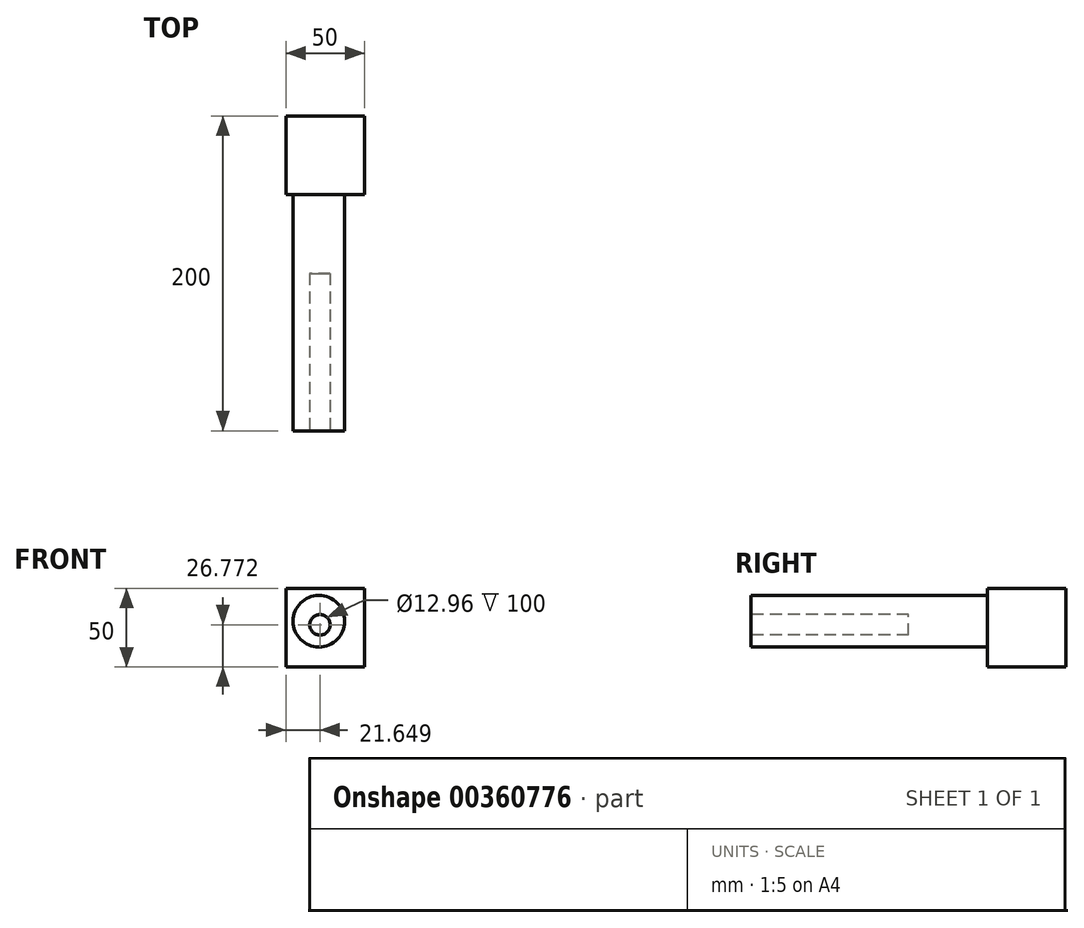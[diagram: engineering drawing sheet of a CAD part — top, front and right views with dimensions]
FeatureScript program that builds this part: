
annotation { "Feature Type Name" : "Feature", "Feature Type Description" : "" }
export const myFeature = defineFeature(function(context is Context, id is Id, definition is map)
    precondition{}
    {
        {
            var Q0;
            Q0=qCreatedBy(makeId("Top.planeOp"),FACE);
            var sketch = newSketch(context, id + "F0", { "sketchPlane" : qUnion([Q0])});
            skLineSegment(sketch, "E0.bottom", {"start": v(0, 0) * mm, "end": v(50, 0) * mm});
            skLineSegment(sketch, "E0.top", {"start": v(0, 50) * mm, "end": v(50, 50) * mm});
            skLineSegment(sketch, "E0.left", {"start": v(0, 0) * mm, "end": v(0, 50) * mm});
            skLineSegment(sketch, "E0.right", {"start": v(50, 0) * mm, "end": v(50, 50) * mm});
            skSolve(sketch);
        }
        {
            var Q0;
            Q0=makeQuery(id+"F0.imprint","IMPRINT",FACE,{"disambiguationData":[TD([[makeQuery(id+"F0.imprint","IMPRINT",EDGE,{"derivedFrom":sQuery(id+"F0.wireOp",EDGE,"E0.bottom")}),1.0]])]});
            extrude(context, id + "F1", {"entities" : qUnion([Q0]), "depth" : 50 * mm});
        }
        {
            var Q0;
            Q0=makeQuery(id+"F1.opExtrude","CAP_FACE",FACE,{"disambiguationData":[OSD([sQuery(id+"F0.wireOp",EDGE,"E0.bottom"),sQuery(id+"F0.wireOp",EDGE,"E0.top"),sQuery(id+"F0.wireOp",EDGE,"E0.left"),sQuery(id+"F0.wireOp",EDGE,"E0.right")])],"isStart":true});
            var sketch = newSketch(context, id + "F2", { "sketchPlane" : qUnion([Q0])});
            skText(sketch, "E1", { "text": "L4zy", "fontName": "OpenSans-Regular.ttf"});
            const initialGuessF2  = {"E1": [0.01875, -0.03184, 1, 0, 0.00952]};
            skSetInitialGuess(sketch, initialGuessF2);
            skSolve(sketch);
        }
        {
            var Q0;
            Q0=makeQuery(id+"F1.opExtrude","SWEPT_FACE",FACE,{"disambiguationData":[OSD([sQuery(id+"F0.wireOp",EDGE,"E0.bottom")])]});
            var sketch = newSketch(context, id + "F3", { "sketchPlane" : qUnion([Q0])});
            skCircle(sketch, "E2", {"center": v(20.99, 29.08) * mm, "radius": 16.43 * mm});
            skSolve(sketch);
        }
        {
            var Q0;
            Q0 = qSketchRegion(id + "F3", true);
            extrude(context, id + "F4", {"entities" : qUnion([Q0]), "operationType" : NewBodyOperationType.ADD, "depth" : 150 * mm});
        }
        {
            var Q0;
            Q0=makeQuery(id+"F4.opExtrude","CAP_FACE",FACE,{"disambiguationData":[OSD([sQuery(id+"F3.wireOp",EDGE,"E2")])],"isStart":false});
            var sketch = newSketch(context, id + "F5", { "sketchPlane" : qUnion([Q0])});
            skCircle(sketch, "E3", {"center": v(21.65, 26.77) * mm, "radius": 6.48 * mm});
            skSolve(sketch);
        }
        {
            var Q0;
            Q0 = qSketchRegion(id + "F5", true);
            extrude(context, id + "F6", {"entities" : qUnion([Q0]), "operationType" : NewBodyOperationType.REMOVE, "oppositeDirection" : true, "depth" : 100 * mm});
        }
    });
